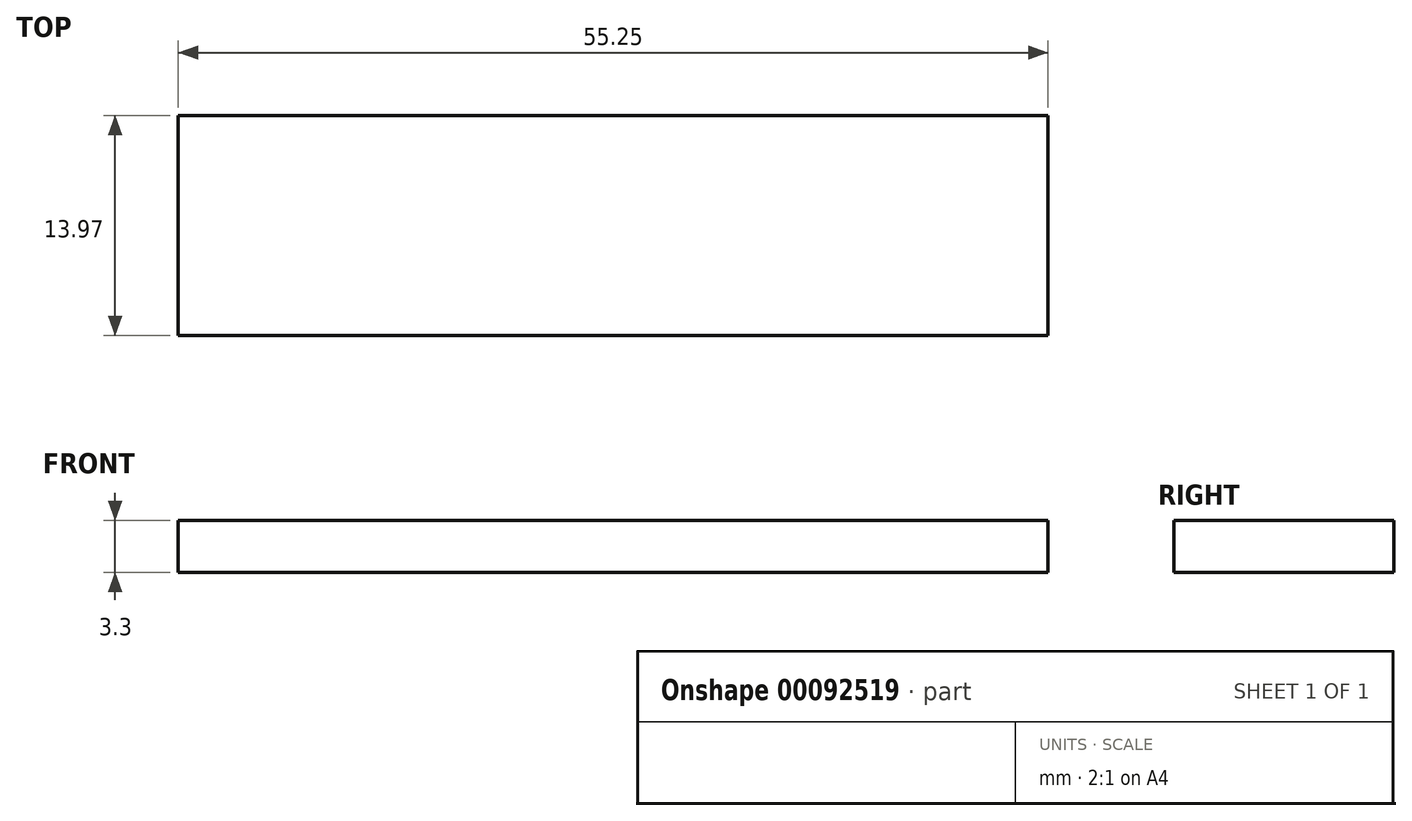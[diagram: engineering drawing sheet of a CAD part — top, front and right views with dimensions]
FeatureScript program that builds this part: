
annotation { "Feature Type Name" : "Feature", "Feature Type Description" : "" }
export const myFeature = defineFeature(function(context is Context, id is Id, definition is map)
    precondition{}
    {
        {
            var Q0;
            Q0=qCreatedBy(makeId("Top.planeOp"),FACE);
            var sketch = newSketch(context, id + "F0", { "sketchPlane" : qUnion([Q0])});
            skLineSegment(sketch, "E0.bottom", {"start": v(0, 0) * mm, "end": v(-55.25, 0) * mm});
            skLineSegment(sketch, "E0.top", {"start": v(0, 13.97) * mm, "end": v(-55.25, 13.97) * mm});
            skLineSegment(sketch, "E0.left", {"start": v(0, 0) * mm, "end": v(0, 13.97) * mm});
            skLineSegment(sketch, "E0.right", {"start": v(-55.25, 0) * mm, "end": v(-55.25, 13.97) * mm});
            skSolve(sketch);
        }
        {
            var Q0;
            Q0=makeQuery(id+"F0.imprint","IMPRINT",FACE,{"disambiguationData":[TD([[makeQuery(id+"F0.imprint","IMPRINT",EDGE,{"derivedFrom":sQuery(id+"F0.wireOp",EDGE,"E0.bottom")}),-1.0]])]});
            extrude(context, id + "F1", {"entities" : qUnion([Q0]), "depth" : 3.3 * mm});
        }
    });
